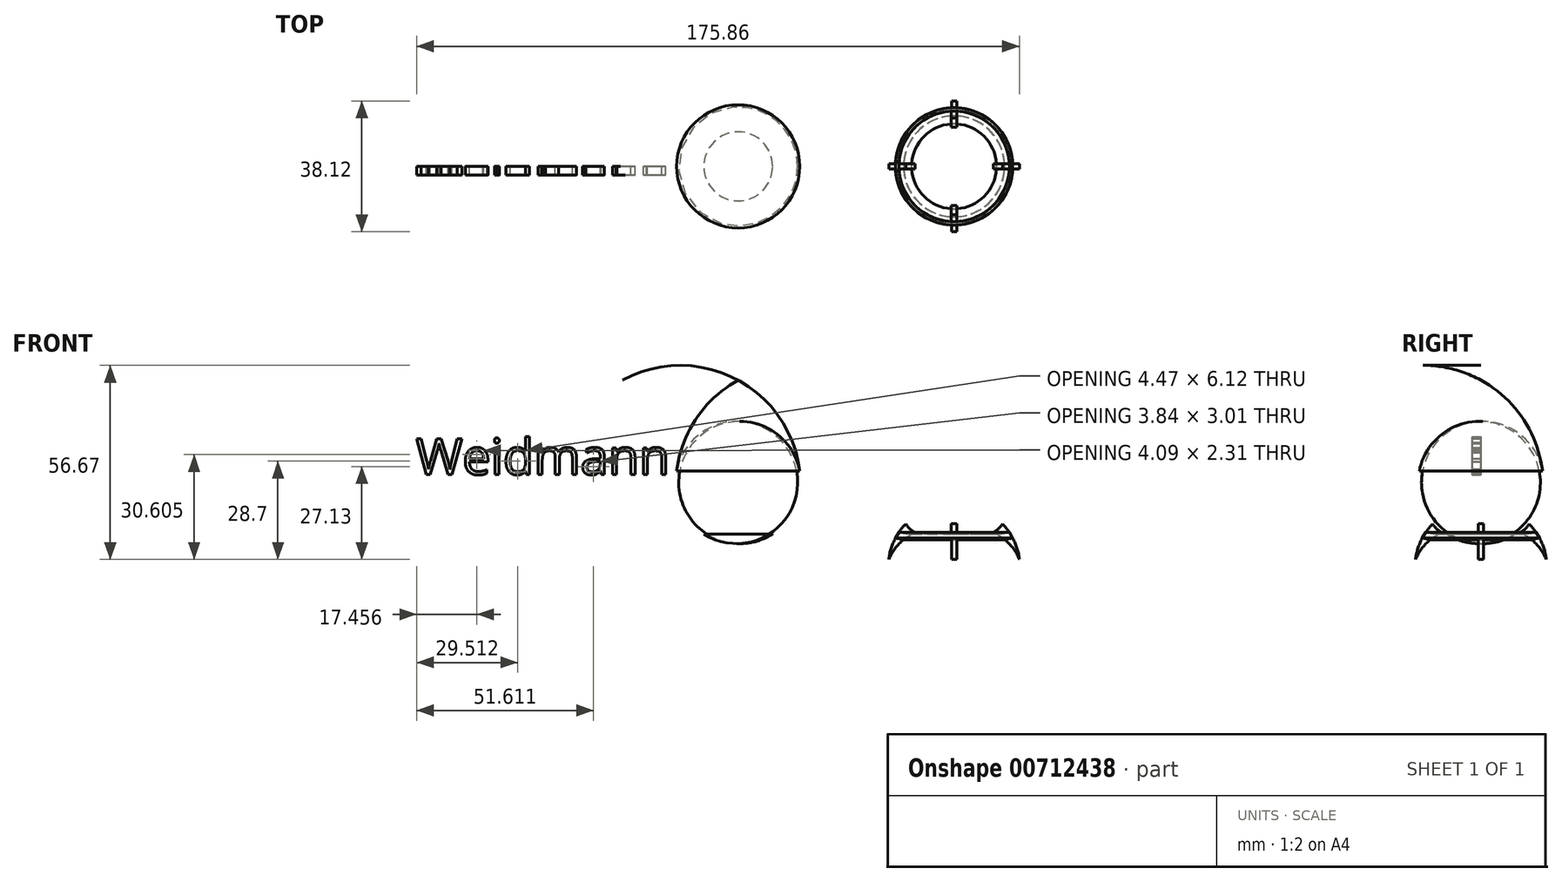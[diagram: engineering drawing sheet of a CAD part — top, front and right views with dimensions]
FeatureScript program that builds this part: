
annotation { "Feature Type Name" : "Feature", "Feature Type Description" : "" }
export const myFeature = defineFeature(function(context is Context, id is Id, definition is map)
    precondition{}
    {
        {
            var Q0;
            Q0=qCreatedBy(makeId("Front.planeOp"),FACE);
            var sketch = newSketch(context, id + "F0", { "sketchPlane" : qUnion([Q0])});
            skArc(sketch, "E0", {"start": v(-17.97, 18.34) * mm, "mid": v(-16.82, 7.96) * mm, "end": v(-10.05, 0) * mm});
            skArc(sketch, "E1", {"start": v(0, 44.9) * mm, "mid": v(-12.2, 33.79) * mm, "end": v(-17.97, 18.34) * mm});
            skLineSegment(sketch, "E2", {"start": v(-10.05, 0) * mm, "end": v(0, 0) * mm});
            skLineSegment(sketch, "E3", {"start": v(0, 0) * mm, "end": v(0, 44.9) * mm});
            skSolve(sketch);
        }
        {
            var Q0;
            Q0=makeQuery(id+"F0.imprint","IMPRINT",FACE,{"disambiguationData":[TD([[makeQuery(id+"F0.imprint","IMPRINT",EDGE,{"derivedFrom":sQuery(id+"F0.wireOp",EDGE,"E0")}),1.0]])]});
            var Q1;
            Q1=sQuery(id+"F0.wireOp",EDGE,"E3");
            revolve(context, id + "F1", {"surfaceOperationType" : NewSurfaceOperationType.NEW, "entities" : qUnion([Q0]), "axis" : qUnion([Q1]), "revolveType" : RevolveType.FULL});
        }
        {
            var Q0;
            Q0=qCreatedBy(makeId("Front.planeOp"),FACE);
            var sketch = newSketch(context, id + "F2", { "sketchPlane" : qUnion([Q0])});
            skArc(sketch, "E4", {"start": v(-14.08, 2.97) * mm, "mid": v(-12.91, 1.5) * mm, "end": v(-11.4, 0.38) * mm});
            skArc(sketch, "E5", {"start": v(-14.08, 2.97) * mm, "mid": v(-17.44, -1.82) * mm, "end": v(-19.06, -7.45) * mm});
            skArc(sketch, "E6", {"start": v(-11.4, 0.38) * mm, "mid": v(-16, -2.77) * mm, "end": v(-19.06, -7.45) * mm});
            skLineSegment(sketch, "E7", {"start": v(-16.14, 0.45) * mm, "end": v(-12.4, -0.08) * mm});
            skLineSegment(sketch, "E8", {"start": v(-12.4, -0.08) * mm, "end": v(-14.74, -1.62) * mm});
            skLineSegment(sketch, "E9", {"start": v(-14.74, -1.62) * mm, "end": v(-17.1, -1.16) * mm});
            skLineSegment(sketch, "E10", {"start": v(-17.1, -1.16) * mm, "end": v(-16.14, 0.45) * mm});
            skLineSegment(sketch, "E11", {"start": v(0, -1.04) * mm, "end": v(0, 1.57) * mm});
            skLineSegment(sketch, "E12", {"start": v(0, 1.57) * mm, "end": v(0, -1.04) * mm});
            skSolve(sketch);
        }
        {
            var Q0;
            {var subQ1=sQuery(id+"F2.wireOp",EDGE,"E7");Q0=makeQuery(id+"F2.imprint","IMPRINT",FACE,{"disambiguationData":[TD([[makeQuery(id+"F2.imprint","IMPRINT",EDGE,{"derivedFrom":subQ1}),-1.0]])]});}
            var Q1;
            Q1=sQuery(id+"F2.wireOp",EDGE,"E12");
            revolve(context, id + "F3", {"surfaceOperationType" : NewSurfaceOperationType.NEW, "entities" : qUnion([Q0]), "axis" : qUnion([Q1]), "revolveType" : RevolveType.FULL});
        }
        {
            var Q0;
            {var subQ3=sQuery(id+"F2.wireOp",EDGE,"E9");Q0=makeQuery(id+"F2.imprint","IMPRINT",FACE,{"disambiguationData":[TD([[makeQuery(id+"F2.imprint","IMPRINT",EDGE,{"derivedFrom":subQ3}),1.0]])]});}
            extrude(context, id + "F4", {"entities" : qUnion([Q0]), "operationType" : NewBodyOperationType.ADD, "endBound" : BoundingType.SYMMETRIC, "depth" : 1.47 * mm, "offsetDistance" : 25.4 * mm});
        }
        {
            var Q0;
            {var subQ0=sQuery(id+"F2.wireOp",EDGE,"E4");Q0=makeQuery(id+"F2.imprint","IMPRINT",FACE,{"disambiguationData":[TD([[makeQuery(id+"F2.imprint","IMPRINT",EDGE,{"derivedFrom":subQ0}),-1.0]])]});}
            extrude(context, id + "F5", {"entities" : qUnion([Q0]), "operationType" : NewBodyOperationType.ADD, "endBound" : BoundingType.SYMMETRIC, "depth" : 1.63 * mm, "offsetDistance" : 25.4 * mm});
        }
        {
            var Q0;
            Q0=makeQuery(id+"F3.opRevolve","SWEPT_BODY",BODY,{"disambiguationData":[OSD([sQuery(id+"F2.wireOp",EDGE,"E6"),sQuery(id+"F2.wireOp",EDGE,"E7"),sQuery(id+"F2.wireOp",EDGE,"E9"),sQuery(id+"F2.wireOp",EDGE,"E10")])]});
            var Q1;
            Q1=sQuery(id+"F2.wireOp",EDGE,"E12");
            circularPattern(context, id + "F6", {"entities" : qUnion([Q0]), "axis" : qUnion([Q1]), "angle" : 360 * degree, "instanceCount" : 4, "equalSpace" : true});
        }
        {
            var Q0;
            Q0=qCreatedBy(makeId("Front.planeOp"),FACE);
            var sketch = newSketch(context, id + "F7", { "sketchPlane" : qUnion([Q0])});
            skLineSegment(sketch, "E13.bottom", {"start": v(-29.04, 69.51) * mm, "end": v(36.04, 69.51) * mm, "construction": true});
            skLineSegment(sketch, "E13.top", {"start": v(-29.04, -49.87) * mm, "end": v(36.04, -49.87) * mm, "construction": true});
            skLineSegment(sketch, "E13.left", {"start": v(-29.04, 69.51) * mm, "end": v(-29.04, -49.87) * mm, "construction": true});
            skLineSegment(sketch, "E13.right", {"start": v(36.04, 69.51) * mm, "end": v(36.04, -49.87) * mm, "construction": true});
            skArc(sketch, "E14", {"start": v(-17.95, 18.37) * mm, "mid": v(-16.85, 7.96) * mm, "end": v(-10.06, 0) * mm});
            skArc(sketch, "E15", {"start": v(0, 44.86) * mm, "mid": v(-12.22, 33.81) * mm, "end": v(-17.95, 18.37) * mm});
            skSolve(sketch);
        }
        {
            var Q0;
            Q0=qCreatedBy(makeId("Front.planeOp"),FACE);
            var sketch = newSketch(context, id + "F8", { "sketchPlane" : qUnion([Q0])});
            skArc(sketch, "E16", {"start": v(0, 47.98) * mm, "mid": v(-1.65, 45.96) * mm, "end": v(-2.33, 43.44) * mm});
            skLineSegment(sketch, "E17", {"start": v(0, 47.98) * mm, "end": v(0, 43.57) * mm});
            skLineSegment(sketch, "E18", {"start": v(-2.33, 43.44) * mm, "end": v(0, 43.57) * mm});
            skSolve(sketch);
        }
        {
            var Q0;
            Q0=makeQuery(id+"F6.opPattern","COPY",BODY,{"derivedFrom":makeQuery(id+"F3.opRevolve","SWEPT_BODY",BODY,{"disambiguationData":[OSD([sQuery(id+"F2.wireOp",EDGE,"E6"),sQuery(id+"F2.wireOp",EDGE,"E7"),sQuery(id+"F2.wireOp",EDGE,"E9"),sQuery(id+"F2.wireOp",EDGE,"E10")])]}),"instanceName":"1"});
            var Q1;
            Q1=makeQuery(id+"F6.opPattern","COPY",BODY,{"derivedFrom":makeQuery(id+"F3.opRevolve","SWEPT_BODY",BODY,{"disambiguationData":[OSD([sQuery(id+"F2.wireOp",EDGE,"E6"),sQuery(id+"F2.wireOp",EDGE,"E7"),sQuery(id+"F2.wireOp",EDGE,"E9"),sQuery(id+"F2.wireOp",EDGE,"E10")])]}),"instanceName":"3"});
            var Q2;
            Q2=makeQuery(id+"F3.opRevolve","SWEPT_BODY",BODY,{"disambiguationData":[OSD([sQuery(id+"F2.wireOp",EDGE,"E6"),sQuery(id+"F2.wireOp",EDGE,"E7"),sQuery(id+"F2.wireOp",EDGE,"E9"),sQuery(id+"F2.wireOp",EDGE,"E10")])]});
            var Q3;
            Q3=makeQuery(id+"F6.opPattern","COPY",BODY,{"derivedFrom":makeQuery(id+"F3.opRevolve","SWEPT_BODY",BODY,{"disambiguationData":[OSD([sQuery(id+"F2.wireOp",EDGE,"E6"),sQuery(id+"F2.wireOp",EDGE,"E7"),sQuery(id+"F2.wireOp",EDGE,"E9"),sQuery(id+"F2.wireOp",EDGE,"E10")])]}),"instanceName":"2"});
            transform(context, id + "F9", {"entities" : qUnion([Q0, Q1, Q2, Q3]), "transformType" : TransformType.TRANSLATION_3D, "dx" : 63 * mm, "dy" : 0 * mm, "dz" : 0 * mm, "makeCopy" : false});
        }
        {
            var Q0;
            Q0=qCreatedBy(makeId("Front.planeOp"),FACE);
            var sketch = newSketch(context, id + "F10", { "sketchPlane" : qUnion([Q0])});
            skText(sketch, "E19", { "text": "Weidmann", "fontName": "OpenSans-Regular.ttf"});
            const initialGuessF10  = {"E19": [-0.094, 0.01734, 1, 0, 0.01052]};
            skSetInitialGuess(sketch, initialGuessF10);
            skSolve(sketch);
        }
        {
            var Q0;
            Q0 = qSketchRegion(id + "F10", true);
            extrude(context, id + "F11", {"entities" : qUnion([Q0]), "depth" : 2.54 * mm, "offsetDistance" : 25.4 * mm});
        }
    });
